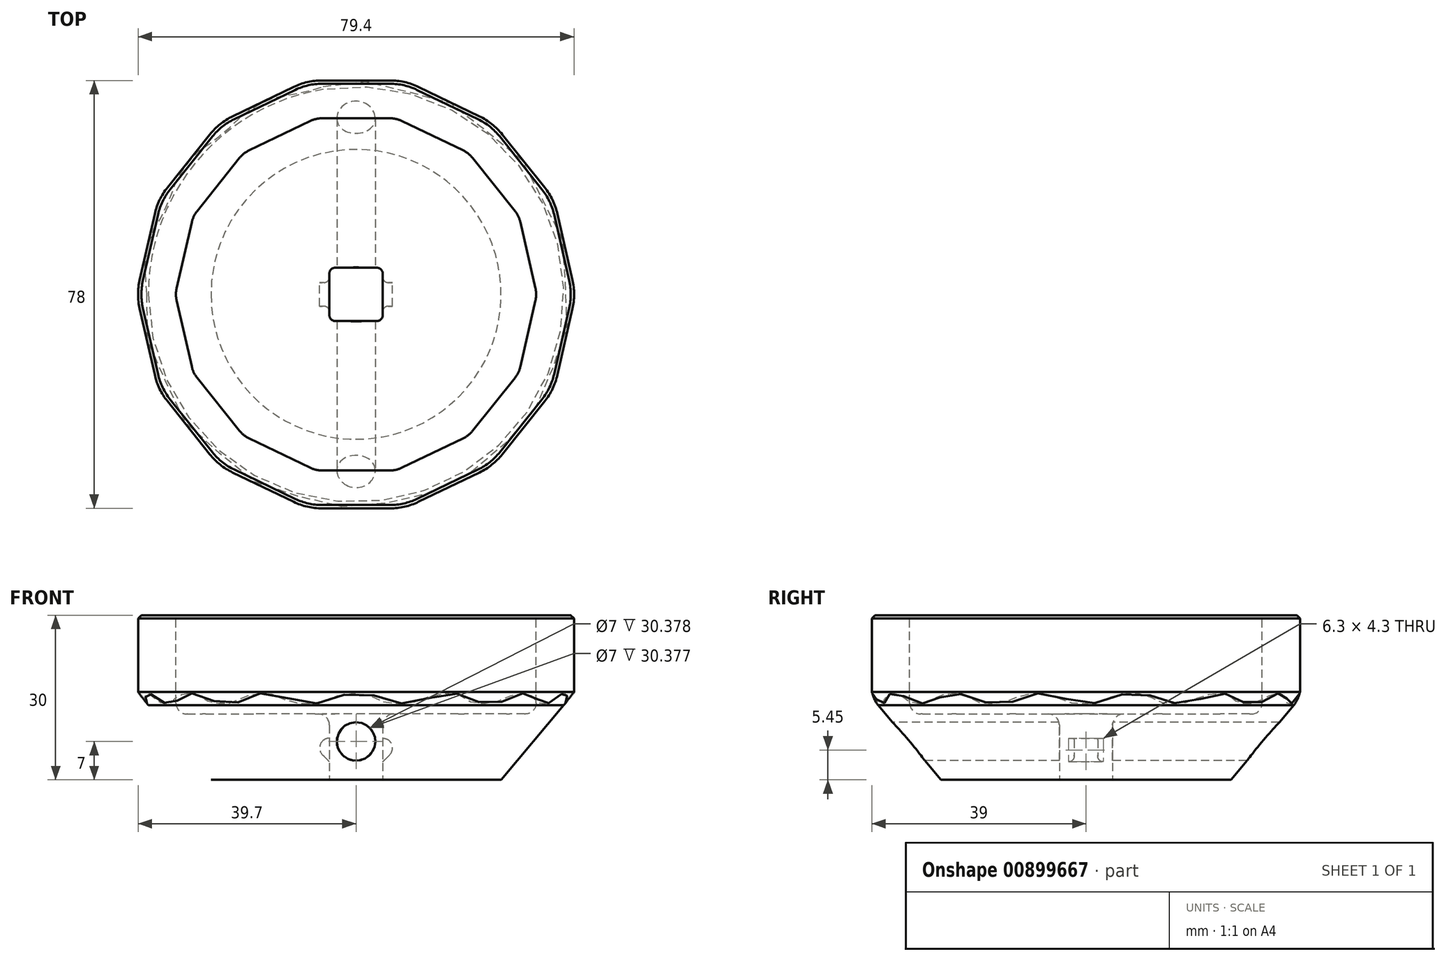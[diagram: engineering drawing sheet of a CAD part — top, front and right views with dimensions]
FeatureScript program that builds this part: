
annotation { "Feature Type Name" : "Feature", "Feature Type Description" : "" }
export const myFeature = defineFeature(function(context is Context, id is Id, definition is map)
    precondition{}
    {
        {
            var Q0;
            Q0=qCreatedBy(makeId("Top.planeOp"),FACE);
            var sketch = newSketch(context, id + "F0", { "sketchPlane" : qUnion([Q0])});
            skLineSegment(sketch, "E0.bottom", {"start": v(3.85, 4.85) * mm, "end": v(-3.85, 4.85) * mm});
            skLineSegment(sketch, "E0.top", {"start": v(3.85, -4.85) * mm, "end": v(-3.85, -4.85) * mm});
            skLineSegment(sketch, "E0.left", {"start": v(4.85, 3.85) * mm, "end": v(4.85, -3.85) * mm});
            skLineSegment(sketch, "E0.right", {"start": v(-4.85, 3.85) * mm, "end": v(-4.85, -3.85) * mm});
            skPoint(sketch, "E0.middle", {"position": v(0, 0) * mm});
            skPoint(sketch, "E1.visualSharp", {"position": v(-4.85, -4.85) * mm});
            skArc(sketch, "E1.filletArc", {"start": v(-4.85, -3.85) * mm, "mid": v(-4.56, -4.56) * mm, "end": v(-3.85, -4.85) * mm});
            skPoint(sketch, "E2.visualSharp", {"position": v(4.85, -4.85) * mm});
            skArc(sketch, "E2.filletArc", {"start": v(3.85, -4.85) * mm, "mid": v(4.56, -4.56) * mm, "end": v(4.85, -3.85) * mm});
            skPoint(sketch, "E3.visualSharp", {"position": v(4.85, 4.85) * mm});
            skArc(sketch, "E3.filletArc", {"start": v(4.85, 3.85) * mm, "mid": v(4.56, 4.56) * mm, "end": v(3.85, 4.85) * mm});
            skPoint(sketch, "E4.visualSharp", {"position": v(-4.85, 4.85) * mm});
            skArc(sketch, "E4.filletArc", {"start": v(-3.85, 4.85) * mm, "mid": v(-4.56, 4.56) * mm, "end": v(-4.85, 3.85) * mm});
            skSolve(sketch);
        }
        {
            var Q0;
            Q0=qCreatedBy(makeId("Front.planeOp"),FACE);
            var sketch = newSketch(context, id + "F1", { "sketchPlane" : qUnion([Q0])});
            skLineSegment(sketch, "E5", {"start": v(0, 0) * mm, "end": v(0, 30) * mm});
            skLineSegment(sketch, "E6", {"start": v(0, 30) * mm, "end": v(-39, 30) * mm});
            skLineSegment(sketch, "E7", {"start": v(-39, 30) * mm, "end": v(-39, 16.82) * mm});
            skLineSegment(sketch, "E8", {"start": v(-37.83, 13.6) * mm, "end": v(-26.41, 0) * mm});
            skLineSegment(sketch, "E9", {"start": v(-26.41, 0) * mm, "end": v(0, 0) * mm});
            skLineSegment(sketch, "E10", {"start": v(0, 0) * mm, "end": v(0, -5.87) * mm, "construction": true});
            skPoint(sketch, "E11.visualSharp", {"position": v(-39, 15) * mm});
            skArc(sketch, "E11.filletArc", {"start": v(-39, 16.82) * mm, "mid": v(-38.7, 15.1) * mm, "end": v(-37.83, 13.6) * mm});
            skSolve(sketch);
        }
        {
            var Q0;
            Q0=qSketchRegion(id+"F1",true);
            var Q1;
            Q1=sQuery(id+"F1.wireOp",EDGE,"E5");
            revolve(context, id + "F2", {"surfaceOperationType" : NewSurfaceOperationType.NEW, "entities" : qUnion([Q0]), "axis" : qUnion([Q1]), "revolveType" : RevolveType.FULL});
        }
        {
            var Q0;
            Q0=qSketchRegion(id+"F0",true);
            extrude(context, id + "F3", {"entities" : qUnion([Q0]), "operationType" : NewBodyOperationType.REMOVE, "endBound" : BoundingType.THROUGH_ALL, "depth" : 12 * mm, "offsetDistance" : 25 * mm});
        }
        {
            var Q0;
            Q0=makeQuery(id+"F2.opRevolve","SWEPT_FACE",FACE,{"disambiguationData":[OSD([sQuery(id+"F1.wireOp",EDGE,"E6")])]});
            var sketch = newSketch(context, id + "F4", { "sketchPlane" : qUnion([Q0])});
            skCircle(sketch, "E12.cCircle", {"center": v(0, 0) * mm, "radius": 32.93 * mm, "construction": true});
            skLineSegment(sketch, "E12.0", {"start": v(21.24, 24.85) * mm, "end": v(28.95, 15.18) * mm});
            skLineSegment(sketch, "E12.1", {"start": v(29.92, 13.17) * mm, "end": v(32.67, 1.11) * mm});
            skLineSegment(sketch, "E12.2", {"start": v(32.67, -1.11) * mm, "end": v(29.92, -13.17) * mm});
            skLineSegment(sketch, "E12.3", {"start": v(28.95, -15.18) * mm, "end": v(21.24, -24.85) * mm});
            skLineSegment(sketch, "E12.4", {"start": v(19.5, -26.24) * mm, "end": v(8.35, -31.6) * mm});
            skLineSegment(sketch, "E12.5", {"start": v(6.19, -32.1) * mm, "end": v(-6.19, -32.1) * mm});
            skLineSegment(sketch, "E12.6", {"start": v(-8.35, -31.6) * mm, "end": v(-19.5, -26.24) * mm});
            skLineSegment(sketch, "E12.7", {"start": v(-21.24, -24.85) * mm, "end": v(-28.95, -15.18) * mm});
            skLineSegment(sketch, "E12.8", {"start": v(-29.92, -13.17) * mm, "end": v(-32.67, -1.11) * mm});
            skLineSegment(sketch, "E12.9", {"start": v(-32.67, 1.11) * mm, "end": v(-29.92, 13.17) * mm});
            skLineSegment(sketch, "E12.10", {"start": v(-28.95, 15.18) * mm, "end": v(-21.24, 24.85) * mm});
            skLineSegment(sketch, "E12.11", {"start": v(-19.5, 26.24) * mm, "end": v(-8.35, 31.6) * mm});
            skLineSegment(sketch, "E12.12", {"start": v(-6.19, 32.1) * mm, "end": v(6.19, 32.1) * mm});
            skLineSegment(sketch, "E12.13", {"start": v(8.35, 31.6) * mm, "end": v(19.5, 26.24) * mm});
            skPoint(sketch, "E13.visualSharp", {"position": v(32.93, 0) * mm});
            skArc(sketch, "E13.filletArc", {"start": v(32.67, -1.11) * mm, "mid": v(32.8, 0) * mm, "end": v(32.67, 1.11) * mm});
            skPoint(sketch, "E14.visualSharp", {"position": v(29.66, -14.29) * mm});
            skArc(sketch, "E14.filletArc", {"start": v(28.95, -15.18) * mm, "mid": v(29.55, -14.23) * mm, "end": v(29.92, -13.17) * mm});
            skPoint(sketch, "E15.visualSharp", {"position": v(29.66, 14.29) * mm});
            skArc(sketch, "E15.filletArc", {"start": v(29.92, 13.17) * mm, "mid": v(29.55, 14.23) * mm, "end": v(28.95, 15.18) * mm});
            skPoint(sketch, "E16.visualSharp", {"position": v(20.53, 25.74) * mm});
            skArc(sketch, "E16.filletArc", {"start": v(21.24, 24.85) * mm, "mid": v(20.45, 25.64) * mm, "end": v(19.5, 26.24) * mm});
            skPoint(sketch, "E17.visualSharp", {"position": v(7.33, 32.1) * mm});
            skArc(sketch, "E17.filletArc", {"start": v(8.35, 31.6) * mm, "mid": v(7.3, 31.97) * mm, "end": v(6.19, 32.1) * mm});
            skPoint(sketch, "E18.visualSharp", {"position": v(-7.33, 32.1) * mm});
            skArc(sketch, "E18.filletArc", {"start": v(-6.19, 32.1) * mm, "mid": v(-7.3, 31.97) * mm, "end": v(-8.35, 31.6) * mm});
            skPoint(sketch, "E19.visualSharp", {"position": v(-20.53, 25.74) * mm});
            skArc(sketch, "E19.filletArc", {"start": v(-19.5, 26.24) * mm, "mid": v(-20.45, 25.64) * mm, "end": v(-21.24, 24.85) * mm});
            skPoint(sketch, "E20.visualSharp", {"position": v(-29.66, 14.29) * mm});
            skArc(sketch, "E20.filletArc", {"start": v(-28.95, 15.18) * mm, "mid": v(-29.55, 14.23) * mm, "end": v(-29.92, 13.17) * mm});
            skPoint(sketch, "E21.visualSharp", {"position": v(-32.93, 0) * mm});
            skArc(sketch, "E21.filletArc", {"start": v(-32.67, 1.11) * mm, "mid": v(-32.8, 0) * mm, "end": v(-32.67, -1.11) * mm});
            skPoint(sketch, "E22.visualSharp", {"position": v(-29.66, -14.29) * mm});
            skArc(sketch, "E22.filletArc", {"start": v(-29.92, -13.17) * mm, "mid": v(-29.55, -14.23) * mm, "end": v(-28.95, -15.18) * mm});
            skPoint(sketch, "E23.visualSharp", {"position": v(-20.53, -25.74) * mm});
            skArc(sketch, "E23.filletArc", {"start": v(-21.24, -24.85) * mm, "mid": v(-20.45, -25.64) * mm, "end": v(-19.5, -26.24) * mm});
            skPoint(sketch, "E24.visualSharp", {"position": v(-7.33, -32.1) * mm});
            skArc(sketch, "E24.filletArc", {"start": v(-8.35, -31.6) * mm, "mid": v(-7.3, -31.97) * mm, "end": v(-6.19, -32.1) * mm});
            skPoint(sketch, "E25.visualSharp", {"position": v(7.33, -32.1) * mm});
            skArc(sketch, "E25.filletArc", {"start": v(6.19, -32.1) * mm, "mid": v(7.3, -31.97) * mm, "end": v(8.35, -31.6) * mm});
            skPoint(sketch, "E26.visualSharp", {"position": v(20.53, -25.74) * mm});
            skArc(sketch, "E26.filletArc", {"start": v(19.5, -26.24) * mm, "mid": v(20.45, -25.64) * mm, "end": v(21.24, -24.85) * mm});
            skSolve(sketch);
        }
        {
            var Q0;
            Q0=makeQuery(id+"F4.imprint","IMPRINT",FACE,{"disambiguationData":[TD([[makeQuery(id+"F4.imprint","IMPRINT",EDGE,{"derivedFrom":sQuery(id+"F4.wireOp",EDGE,"E12.0")}),1.0]])]});
            var sketch = newSketch(context, id + "F5", { "sketchPlane" : qUnion([Q0])});
            skCircle(sketch, "E27.0", {"center": v(0, 0) * mm, "radius": 32.93 * mm, "construction": true});
            skLineSegment(sketch, "E27.1", {"start": v(21.24, 24.85) * mm, "end": v(28.95, 15.18) * mm});
            skLineSegment(sketch, "E27.2", {"start": v(29.92, 13.17) * mm, "end": v(32.67, 1.11) * mm});
            skLineSegment(sketch, "E27.3", {"start": v(32.67, -1.11) * mm, "end": v(29.92, -13.17) * mm});
            skLineSegment(sketch, "E27.4", {"start": v(28.95, -15.18) * mm, "end": v(21.24, -24.85) * mm});
            skLineSegment(sketch, "E27.5", {"start": v(19.5, -26.24) * mm, "end": v(8.35, -31.6) * mm});
            skLineSegment(sketch, "E27.6", {"start": v(6.19, -32.1) * mm, "end": v(-6.19, -32.1) * mm});
            skLineSegment(sketch, "E27.7", {"start": v(-8.35, -31.6) * mm, "end": v(-19.5, -26.24) * mm});
            skLineSegment(sketch, "E27.8", {"start": v(-21.24, -24.85) * mm, "end": v(-28.95, -15.18) * mm});
            skLineSegment(sketch, "E27.9", {"start": v(-29.92, -13.17) * mm, "end": v(-32.67, -1.11) * mm});
            skLineSegment(sketch, "E27.10", {"start": v(-32.67, 1.11) * mm, "end": v(-29.92, 13.17) * mm});
            skLineSegment(sketch, "E27.11", {"start": v(-28.95, 15.18) * mm, "end": v(-21.24, 24.85) * mm});
            skLineSegment(sketch, "E27.12", {"start": v(-19.5, 26.24) * mm, "end": v(-8.35, 31.6) * mm});
            skLineSegment(sketch, "E27.13", {"start": v(-6.19, 32.1) * mm, "end": v(6.19, 32.1) * mm});
            skLineSegment(sketch, "E27.14", {"start": v(8.35, 31.6) * mm, "end": v(19.5, 26.24) * mm});
            skPoint(sketch, "E27.15", {"position": v(32.93, 0) * mm});
            skArc(sketch, "E27.16", {"start": v(32.67, -1.11) * mm, "mid": v(32.8, 0) * mm, "end": v(32.67, 1.11) * mm});
            skPoint(sketch, "E27.17", {"position": v(29.66, -14.29) * mm});
            skArc(sketch, "E27.18", {"start": v(28.95, -15.18) * mm, "mid": v(29.55, -14.23) * mm, "end": v(29.92, -13.17) * mm});
            skPoint(sketch, "E27.19", {"position": v(29.66, 14.29) * mm});
            skArc(sketch, "E27.20", {"start": v(29.92, 13.17) * mm, "mid": v(29.55, 14.23) * mm, "end": v(28.95, 15.18) * mm});
            skPoint(sketch, "E27.21", {"position": v(20.53, 25.74) * mm});
            skArc(sketch, "E27.22", {"start": v(21.24, 24.85) * mm, "mid": v(20.45, 25.64) * mm, "end": v(19.5, 26.24) * mm});
            skPoint(sketch, "E27.23", {"position": v(7.33, 32.1) * mm});
            skArc(sketch, "E27.24", {"start": v(8.35, 31.6) * mm, "mid": v(7.3, 31.97) * mm, "end": v(6.19, 32.1) * mm});
            skPoint(sketch, "E27.25", {"position": v(-7.33, 32.1) * mm});
            skArc(sketch, "E27.26", {"start": v(-6.19, 32.1) * mm, "mid": v(-7.3, 31.97) * mm, "end": v(-8.35, 31.6) * mm});
            skPoint(sketch, "E27.27", {"position": v(-20.53, 25.74) * mm});
            skArc(sketch, "E27.28", {"start": v(-19.5, 26.24) * mm, "mid": v(-20.45, 25.64) * mm, "end": v(-21.24, 24.85) * mm});
            skPoint(sketch, "E27.29", {"position": v(-29.66, 14.29) * mm});
            skArc(sketch, "E27.30", {"start": v(-28.95, 15.18) * mm, "mid": v(-29.55, 14.23) * mm, "end": v(-29.92, 13.17) * mm});
            skPoint(sketch, "E27.31", {"position": v(-32.93, 0) * mm});
            skArc(sketch, "E27.32", {"start": v(-32.67, 1.11) * mm, "mid": v(-32.8, 0) * mm, "end": v(-32.67, -1.11) * mm});
            skPoint(sketch, "E27.33", {"position": v(-29.66, -14.29) * mm});
            skArc(sketch, "E27.34", {"start": v(-29.92, -13.17) * mm, "mid": v(-29.55, -14.23) * mm, "end": v(-28.95, -15.18) * mm});
            skPoint(sketch, "E27.35", {"position": v(-20.53, -25.74) * mm});
            skArc(sketch, "E27.36", {"start": v(-21.24, -24.85) * mm, "mid": v(-20.45, -25.64) * mm, "end": v(-19.5, -26.24) * mm});
            skPoint(sketch, "E27.37", {"position": v(-7.33, -32.1) * mm});
            skArc(sketch, "E27.38", {"start": v(-8.35, -31.6) * mm, "mid": v(-7.3, -31.97) * mm, "end": v(-6.19, -32.1) * mm});
            skPoint(sketch, "E27.39", {"position": v(7.33, -32.1) * mm});
            skArc(sketch, "E27.40", {"start": v(6.19, -32.1) * mm, "mid": v(7.3, -31.97) * mm, "end": v(8.35, -31.6) * mm});
            skPoint(sketch, "E27.41", {"position": v(20.53, -25.74) * mm});
            skArc(sketch, "E27.42", {"start": v(19.5, -26.24) * mm, "mid": v(20.45, -25.64) * mm, "end": v(21.24, -24.85) * mm});
            skArc(sketch, "E28.0", {"start": v(-6.19, 39) * mm, "mid": v(-8.83, 38.7) * mm, "end": v(-11.35, 37.82) * mm});
            skLineSegment(sketch, "E28.1", {"start": v(-22.5, 32.45) * mm, "end": v(-11.35, 37.82) * mm});
            skArc(sketch, "E28.2", {"start": v(-22.5, 32.45) * mm, "mid": v(-24.75, 31.04) * mm, "end": v(-26.63, 29.15) * mm});
            skLineSegment(sketch, "E28.3", {"start": v(-34.35, 19.48) * mm, "end": v(-26.63, 29.15) * mm});
            skArc(sketch, "E28.4", {"start": v(-34.35, 19.48) * mm, "mid": v(-35.77, 17.22) * mm, "end": v(-36.65, 14.7) * mm});
            skLineSegment(sketch, "E28.5", {"start": v(34.35, -19.48) * mm, "end": v(26.63, -29.15) * mm});
            skArc(sketch, "E28.6", {"start": v(34.35, -19.48) * mm, "mid": v(35.77, -17.22) * mm, "end": v(36.65, -14.7) * mm});
            skLineSegment(sketch, "E28.7", {"start": v(39.4, -2.65) * mm, "end": v(36.65, -14.7) * mm});
            skArc(sketch, "E28.8", {"start": v(39.4, -2.65) * mm, "mid": v(39.7, 0) * mm, "end": v(39.4, 2.65) * mm});
            skLineSegment(sketch, "E28.9", {"start": v(36.65, 14.7) * mm, "end": v(39.4, 2.65) * mm});
            skArc(sketch, "E28.10", {"start": v(36.65, 14.7) * mm, "mid": v(35.77, 17.22) * mm, "end": v(34.35, 19.48) * mm});
            skArc(sketch, "E28.11", {"start": v(11.35, 37.82) * mm, "mid": v(8.83, 38.7) * mm, "end": v(6.19, 39) * mm});
            skLineSegment(sketch, "E28.12", {"start": v(11.35, 37.82) * mm, "end": v(22.5, 32.45) * mm});
            skArc(sketch, "E28.13", {"start": v(26.63, 29.15) * mm, "mid": v(24.75, 31.04) * mm, "end": v(22.5, 32.45) * mm});
            skLineSegment(sketch, "E28.14", {"start": v(26.63, 29.15) * mm, "end": v(34.35, 19.48) * mm});
            skArc(sketch, "E28.15", {"start": v(22.5, -32.45) * mm, "mid": v(24.75, -31.04) * mm, "end": v(26.63, -29.15) * mm});
            skLineSegment(sketch, "E28.16", {"start": v(22.5, -32.45) * mm, "end": v(11.35, -37.82) * mm});
            skArc(sketch, "E28.17", {"start": v(6.19, -39) * mm, "mid": v(8.83, -38.7) * mm, "end": v(11.35, -37.82) * mm});
            skLineSegment(sketch, "E28.18", {"start": v(6.19, -39) * mm, "end": v(-6.19, -39) * mm});
            skArc(sketch, "E28.19", {"start": v(-11.35, -37.82) * mm, "mid": v(-8.83, -38.7) * mm, "end": v(-6.19, -39) * mm});
            skLineSegment(sketch, "E28.20", {"start": v(-6.19, 39) * mm, "end": v(6.19, 39) * mm});
            skLineSegment(sketch, "E28.21", {"start": v(-11.35, -37.82) * mm, "end": v(-22.5, -32.45) * mm});
            skArc(sketch, "E28.22", {"start": v(-26.63, -29.15) * mm, "mid": v(-24.75, -31.04) * mm, "end": v(-22.5, -32.45) * mm});
            skLineSegment(sketch, "E28.23", {"start": v(-26.63, -29.15) * mm, "end": v(-34.35, -19.48) * mm});
            skArc(sketch, "E28.24", {"start": v(-36.65, -14.7) * mm, "mid": v(-35.77, -17.22) * mm, "end": v(-34.35, -19.48) * mm});
            skLineSegment(sketch, "E28.25", {"start": v(-36.65, -14.7) * mm, "end": v(-39.4, -2.65) * mm});
            skArc(sketch, "E28.26", {"start": v(-39.4, 2.65) * mm, "mid": v(-39.7, 0) * mm, "end": v(-39.4, -2.65) * mm});
            skLineSegment(sketch, "E28.27", {"start": v(-39.4, 2.65) * mm, "end": v(-36.65, 14.7) * mm});
            skSolve(sketch);
        }
        {
            var Q0;
            Q0=qCreatedBy(makeId("Top.planeOp"),FACE);
            var Q1;
            Q1=sQuery(id+"F1.wireOp",VERTEX,"E8.start");
            cPlane(context, id + "F6", {"entities" : qUnion([Q0, Q1]), "cplaneType" : CPlaneType.PLANE_POINT, "offset" : 25 * mm, "width" : 150 * mm, "height" : 150 * mm});
        }
        {
            var Q0;
            Q0=qSketchRegion(id+"F5",true);
            var Q1;
            Q1=makeQuery(id+"F11.boolean.opBoolean","COPY",FACE,{"derivedFrom":makeQuery(id+"F11.opExtrude","CAP_FACE",FACE,{"disambiguationData":[OSD([sQuery(id+"F4.wireOp",EDGE,"E12.0"),sQuery(id+"F4.wireOp",EDGE,"E12.1"),sQuery(id+"F4.wireOp",EDGE,"E12.2"),sQuery(id+"F4.wireOp",EDGE,"E12.3"),sQuery(id+"F4.wireOp",EDGE,"E12.4"),sQuery(id+"F4.wireOp",EDGE,"E12.5"),sQuery(id+"F4.wireOp",EDGE,"E12.6"),sQuery(id+"F4.wireOp",EDGE,"E12.7"),sQuery(id+"F4.wireOp",EDGE,"E12.8"),sQuery(id+"F4.wireOp",EDGE,"E12.9"),sQuery(id+"F4.wireOp",EDGE,"E12.10"),sQuery(id+"F4.wireOp",EDGE,"E12.11"),sQuery(id+"F4.wireOp",EDGE,"E12.12"),sQuery(id+"F4.wireOp",EDGE,"E12.13"),sQuery(id+"F4.wireOp",EDGE,"E13.filletArc"),sQuery(id+"F4.wireOp",EDGE,"E14.filletArc"),sQuery(id+"F4.wireOp",EDGE,"E15.filletArc"),sQuery(id+"F4.wireOp",EDGE,"E16.filletArc"),sQuery(id+"F4.wireOp",EDGE,"E17.filletArc"),sQuery(id+"F4.wireOp",EDGE,"E18.filletArc"),sQuery(id+"F4.wireOp",EDGE,"E19.filletArc"),sQuery(id+"F4.wireOp",EDGE,"E20.filletArc"),sQuery(id+"F4.wireOp",EDGE,"E21.filletArc"),sQuery(id+"F4.wireOp",EDGE,"E22.filletArc"),sQuery(id+"F4.wireOp",EDGE,"E23.filletArc"),sQuery(id+"F4.wireOp",EDGE,"E24.filletArc"),sQuery(id+"F4.wireOp",EDGE,"E25.filletArc"),sQuery(id+"F4.wireOp",EDGE,"E26.filletArc")])],"isStart":false})});
            extrude(context, id + "F7", {"entities" : qUnion([Q0]), "operationType" : NewBodyOperationType.ADD, "oppositeDirection" : true, "depth" : 14 * mm, "endBoundEntityFace" : qUnion([Q1]), "offsetDistance" : 25 * mm});
        }
        {
            var Q0;
            Q0=qCreatedBy(id+"F6.planeOp",FACE);
            var sketch = newSketch(context, id + "F8", { "sketchPlane" : qUnion([Q0])});
            skCircle(sketch, "E29.0", {"center": v(0, 0) * mm, "radius": 37.83 * mm});
            skLineSegment(sketch, "E30", {"start": v(6.19, 39) * mm, "end": v(0, 0) * mm, "construction": true});
            skLineSegment(sketch, "E31", {"start": v(0, 0) * mm, "end": v(11.35, 37.82) * mm, "construction": true});
            skPoint(sketch, "E32.0", {"position": v(11.35, 37.82) * mm});
            skPoint(sketch, "E33.1", {"position": v(6.19, 39) * mm});
            skPoint(sketch, "E34", {"position": v(10.87, 36.23) * mm});
            skPoint(sketch, "E35", {"position": v(5.93, 37.36) * mm});
            skPoint(sketch, "E36.1.0", {"position": v(-5.93, 37.36) * mm});
            skPoint(sketch, "E36.1.1", {"position": v(-10.87, 36.23) * mm});
            skPoint(sketch, "E36.2.0", {"position": v(-21.55, 31.1) * mm});
            skPoint(sketch, "E36.2.1", {"position": v(-25.52, 27.93) * mm});
            skPoint(sketch, "E36.3.0", {"position": v(-32.9, 18.66) * mm});
            skPoint(sketch, "E36.3.1", {"position": v(-35.1, 14.1) * mm});
            skPoint(sketch, "E36.4.0", {"position": v(-37.75, 2.54) * mm});
            skPoint(sketch, "E36.4.1", {"position": v(-37.75, -2.54) * mm});
            skPoint(sketch, "E36.5.0", {"position": v(-35.1, -14.1) * mm});
            skPoint(sketch, "E36.5.1", {"position": v(-32.9, -18.66) * mm});
            skPoint(sketch, "E36.6.0", {"position": v(-25.52, -27.93) * mm});
            skPoint(sketch, "E36.6.1", {"position": v(-21.55, -31.1) * mm});
            skPoint(sketch, "E36.7.0", {"position": v(-10.87, -36.23) * mm});
            skPoint(sketch, "E36.7.1", {"position": v(-5.93, -37.36) * mm});
            skPoint(sketch, "E36.8.0", {"position": v(5.93, -37.36) * mm});
            skPoint(sketch, "E36.8.1", {"position": v(10.87, -36.23) * mm});
            skPoint(sketch, "E36.9.0", {"position": v(21.55, -31.1) * mm});
            skPoint(sketch, "E36.9.1", {"position": v(25.52, -27.93) * mm});
            skPoint(sketch, "E36.10.0", {"position": v(32.9, -18.66) * mm});
            skPoint(sketch, "E36.10.1", {"position": v(35.1, -14.1) * mm});
            skPoint(sketch, "E36.11.0", {"position": v(37.75, -2.54) * mm});
            skPoint(sketch, "E36.11.1", {"position": v(37.75, 2.54) * mm});
            skPoint(sketch, "E36.12.0", {"position": v(35.1, 14.1) * mm});
            skPoint(sketch, "E36.12.1", {"position": v(32.9, 18.66) * mm});
            skPoint(sketch, "E36.13.0", {"position": v(25.52, 27.93) * mm});
            skPoint(sketch, "E36.13.1", {"position": v(21.55, 31.1) * mm});
            skSolve(sketch);
        }
        {
            var Q0;
            Q0=makeQuery(id+"F7.opExtrude","CAP_FACE",FACE,{"disambiguationData":[OSD([sQuery(id+"F5.wireOp",EDGE,"E27.1"),sQuery(id+"F5.wireOp",EDGE,"E27.2"),sQuery(id+"F5.wireOp",EDGE,"E27.3"),sQuery(id+"F5.wireOp",EDGE,"E27.4"),sQuery(id+"F5.wireOp",EDGE,"E27.5"),sQuery(id+"F5.wireOp",EDGE,"E27.6"),sQuery(id+"F5.wireOp",EDGE,"E27.7"),sQuery(id+"F5.wireOp",EDGE,"E27.8"),sQuery(id+"F5.wireOp",EDGE,"E27.9"),sQuery(id+"F5.wireOp",EDGE,"E27.10"),sQuery(id+"F5.wireOp",EDGE,"E27.11"),sQuery(id+"F5.wireOp",EDGE,"E27.12"),sQuery(id+"F5.wireOp",EDGE,"E27.13"),sQuery(id+"F5.wireOp",EDGE,"E27.14"),sQuery(id+"F5.wireOp",EDGE,"E27.16"),sQuery(id+"F5.wireOp",EDGE,"E27.18"),sQuery(id+"F5.wireOp",EDGE,"E27.20"),sQuery(id+"F5.wireOp",EDGE,"E27.22"),sQuery(id+"F5.wireOp",EDGE,"E27.24"),sQuery(id+"F5.wireOp",EDGE,"E27.26"),sQuery(id+"F5.wireOp",EDGE,"E27.28"),sQuery(id+"F5.wireOp",EDGE,"E27.30"),sQuery(id+"F5.wireOp",EDGE,"E27.32"),sQuery(id+"F5.wireOp",EDGE,"E27.34"),sQuery(id+"F5.wireOp",EDGE,"E27.36"),sQuery(id+"F5.wireOp",EDGE,"E27.38"),sQuery(id+"F5.wireOp",EDGE,"E27.40"),sQuery(id+"F5.wireOp",EDGE,"E27.42"),sQuery(id+"F5.wireOp",EDGE,"E28.0"),sQuery(id+"F5.wireOp",EDGE,"E28.1"),sQuery(id+"F5.wireOp",EDGE,"E28.2"),sQuery(id+"F5.wireOp",EDGE,"E28.3"),sQuery(id+"F5.wireOp",EDGE,"E28.4"),sQuery(id+"F5.wireOp",EDGE,"E28.5"),sQuery(id+"F5.wireOp",EDGE,"E28.6"),sQuery(id+"F5.wireOp",EDGE,"E28.7"),sQuery(id+"F5.wireOp",EDGE,"E28.8"),sQuery(id+"F5.wireOp",EDGE,"E28.9"),sQuery(id+"F5.wireOp",EDGE,"E28.10"),sQuery(id+"F5.wireOp",EDGE,"E28.11"),sQuery(id+"F5.wireOp",EDGE,"E28.12"),sQuery(id+"F5.wireOp",EDGE,"E28.13"),sQuery(id+"F5.wireOp",EDGE,"E28.14"),sQuery(id+"F5.wireOp",EDGE,"E28.15"),sQuery(id+"F5.wireOp",EDGE,"E28.16"),sQuery(id+"F5.wireOp",EDGE,"E28.17"),sQuery(id+"F5.wireOp",EDGE,"E28.18"),sQuery(id+"F5.wireOp",EDGE,"E28.19"),sQuery(id+"F5.wireOp",EDGE,"E28.20"),sQuery(id+"F5.wireOp",EDGE,"E28.21"),sQuery(id+"F5.wireOp",EDGE,"E28.22"),sQuery(id+"F5.wireOp",EDGE,"E28.23"),sQuery(id+"F5.wireOp",EDGE,"E28.24"),sQuery(id+"F5.wireOp",EDGE,"E28.25"),sQuery(id+"F5.wireOp",EDGE,"E28.26"),sQuery(id+"F5.wireOp",EDGE,"E28.27")])],"isStart":false});
            var sketch = newSketch(context, id + "F9", { "sketchPlane" : qUnion([Q0])});
            skArc(sketch, "E37.43", {"start": v(-6.19, -39) * mm, "mid": v(-8.83, -38.7) * mm, "end": v(-11.35, -37.82) * mm});
            skLineSegment(sketch, "E37.44", {"start": v(-22.5, -32.45) * mm, "end": v(-11.35, -37.82) * mm});
            skArc(sketch, "E37.45", {"start": v(-22.5, -32.45) * mm, "mid": v(-24.75, -31.04) * mm, "end": v(-26.63, -29.15) * mm});
            skLineSegment(sketch, "E37.46", {"start": v(-34.35, -19.48) * mm, "end": v(-26.63, -29.15) * mm});
            skArc(sketch, "E37.47", {"start": v(-34.35, -19.48) * mm, "mid": v(-35.77, -17.22) * mm, "end": v(-36.65, -14.7) * mm});
            skLineSegment(sketch, "E37.48", {"start": v(34.35, 19.48) * mm, "end": v(26.63, 29.15) * mm});
            skArc(sketch, "E37.49", {"start": v(34.35, 19.48) * mm, "mid": v(35.77, 17.22) * mm, "end": v(36.65, 14.7) * mm});
            skLineSegment(sketch, "E37.50", {"start": v(39.4, 2.65) * mm, "end": v(36.65, 14.7) * mm});
            skArc(sketch, "E37.51", {"start": v(39.4, 2.65) * mm, "mid": v(39.7, 0) * mm, "end": v(39.4, -2.65) * mm});
            skLineSegment(sketch, "E37.52", {"start": v(36.65, -14.7) * mm, "end": v(39.4, -2.65) * mm});
            skArc(sketch, "E37.53", {"start": v(36.65, -14.7) * mm, "mid": v(35.77, -17.22) * mm, "end": v(34.35, -19.48) * mm});
            skArc(sketch, "E37.54", {"start": v(11.35, -37.82) * mm, "mid": v(8.83, -38.7) * mm, "end": v(6.19, -39) * mm});
            skLineSegment(sketch, "E37.55", {"start": v(11.35, -37.82) * mm, "end": v(22.5, -32.45) * mm});
            skArc(sketch, "E37.56", {"start": v(26.63, -29.15) * mm, "mid": v(24.75, -31.04) * mm, "end": v(22.5, -32.45) * mm});
            skLineSegment(sketch, "E37.57", {"start": v(26.63, -29.15) * mm, "end": v(34.35, -19.48) * mm});
            skArc(sketch, "E37.58", {"start": v(22.5, 32.45) * mm, "mid": v(24.75, 31.04) * mm, "end": v(26.63, 29.15) * mm});
            skLineSegment(sketch, "E37.59", {"start": v(22.5, 32.45) * mm, "end": v(11.35, 37.82) * mm});
            skArc(sketch, "E37.60", {"start": v(6.19, 39) * mm, "mid": v(8.83, 38.7) * mm, "end": v(11.35, 37.82) * mm});
            skLineSegment(sketch, "E37.61", {"start": v(6.19, 39) * mm, "end": v(-6.19, 39) * mm});
            skArc(sketch, "E37.62", {"start": v(-11.35, 37.82) * mm, "mid": v(-8.83, 38.7) * mm, "end": v(-6.19, 39) * mm});
            skLineSegment(sketch, "E37.63", {"start": v(-6.19, -39) * mm, "end": v(6.19, -39) * mm});
            skLineSegment(sketch, "E37.64", {"start": v(-11.35, 37.82) * mm, "end": v(-22.5, 32.45) * mm});
            skArc(sketch, "E37.65", {"start": v(-26.63, 29.15) * mm, "mid": v(-24.75, 31.04) * mm, "end": v(-22.5, 32.45) * mm});
            skLineSegment(sketch, "E37.66", {"start": v(-26.63, 29.15) * mm, "end": v(-34.35, 19.48) * mm});
            skArc(sketch, "E37.67", {"start": v(-36.65, 14.7) * mm, "mid": v(-35.77, 17.22) * mm, "end": v(-34.35, 19.48) * mm});
            skLineSegment(sketch, "E37.68", {"start": v(-36.65, 14.7) * mm, "end": v(-39.4, 2.65) * mm});
            skArc(sketch, "E37.69", {"start": v(-39.4, -2.65) * mm, "mid": v(-39.7, 0) * mm, "end": v(-39.4, 2.65) * mm});
            skLineSegment(sketch, "E37.70", {"start": v(-39.4, -2.65) * mm, "end": v(-36.65, -14.7) * mm});
            skSolve(sketch);
        }
        {
            var Q1;
            Q1=qSketchRegion(id+"F9",true);
            var Q2;
            Q2=qSketchRegion(id+"F8",true);
            loft(context, id + "F10", {"operationType" : NewBodyOperationType.ADD, "sheetProfilesArray" : [{ "sheetProfileEntities" : qUnion([Q1]) }, { "sheetProfileEntities" : qUnion([Q2]) }]});
        }
        {
            var Q0;
            Q0=qSketchRegion(id+"F4",true);
            extrude(context, id + "F11", {"entities" : qUnion([Q0]), "operationType" : NewBodyOperationType.REMOVE, "oppositeDirection" : true, "depth" : 18 * mm, "offsetDistance" : 25 * mm});
        }
        {
            var Q0;
            Q0=qCreatedBy(makeId("Front.planeOp"),FACE);
            var sketch = newSketch(context, id + "F12", { "sketchPlane" : qUnion([Q0])});
            skLineSegment(sketch, "E38", {"start": v(-4.85, 7.6) * mm, "end": v(0, 7.6) * mm});
            skLineSegment(sketch, "E39", {"start": v(-4.85, 3.3) * mm, "end": v(0, 3.3) * mm});
            skLineSegment(sketch, "E40", {"start": v(-5.67, 5.45) * mm, "end": v(-0.86, 5.45) * mm, "construction": true});
            skLineSegment(sketch, "E41", {"start": v(-4.85, 3.3) * mm, "end": v(-6.1, 4.56) * mm});
            skArc(sketch, "E42", {"start": v(-4.85, 7.6) * mm, "mid": v(-6.5, 6.5) * mm, "end": v(-6.1, 4.56) * mm});
            skLineSegment(sketch, "E43.MirrorCS", {"start": v(4.85, 7.6) * mm, "end": v(0, 7.6) * mm});
            skArc(sketch, "E44.MirrorCS", {"start": v(4.85, 7.6) * mm, "mid": v(6.5, 6.5) * mm, "end": v(6.1, 4.56) * mm});
            skLineSegment(sketch, "E45.MirrorCS", {"start": v(4.85, 3.3) * mm, "end": v(6.1, 4.56) * mm});
            skLineSegment(sketch, "E46.MirrorCS", {"start": v(4.85, 3.3) * mm, "end": v(0, 3.3) * mm});
            skLineSegment(sketch, "E47.MirrorCS", {"start": v(5.67, 5.45) * mm, "end": v(0.86, 5.45) * mm, "construction": true});
            skSolve(sketch);
        }
        {
            var Q0;
            Q0=qSketchRegion(id+"F12",true);
            extrude(context, id + "F13", {"entities" : qUnion([Q0]), "operationType" : NewBodyOperationType.REMOVE, "endBound" : BoundingType.SYMMETRIC, "depth" : 4.3 * mm, "offsetDistance" : 25 * mm});
        }
        {
            var Q0;
            Q0=makeQuery(id+"F13.boolean.opBoolean","INTERSECT",EDGE,{"derivedFrom":[makeQuery(id+"F3.boolean.opBoolean","COPY",FACE,{"derivedFrom":makeQuery(id+"F3.opExtrude","SWEPT_FACE",FACE,{"disambiguationData":[OSD([sQuery(id+"F0.wireOp",EDGE,"E0.right")])]})}),makeQuery(id+"F13.opExtrude","CAP_FACE",FACE,{"disambiguationData":[OSD([sQuery(id+"F12.wireOp",EDGE,"E38"),sQuery(id+"F12.wireOp",EDGE,"E39"),sQuery(id+"F12.wireOp",EDGE,"E41"),sQuery(id+"F12.wireOp",EDGE,"E42"),sQuery(id+"F12.wireOp",EDGE,"E43.MirrorCS"),sQuery(id+"F12.wireOp",EDGE,"E44.MirrorCS"),sQuery(id+"F12.wireOp",EDGE,"E45.MirrorCS"),sQuery(id+"F12.wireOp",EDGE,"E46.MirrorCS")])],"isStart":false})]});
            var Q1;
            Q1=makeQuery(id+"FJ3eJoukwGj3lDz_1.1.F13.boolean.opBoolean","INTERSECT",EDGE,{"derivedFrom":[makeQuery(id+"F3.boolean.opBoolean","COPY",FACE,{"derivedFrom":makeQuery(id+"F3.opExtrude","SWEPT_FACE",FACE,{"disambiguationData":[OSD([sQuery(id+"F0.wireOp",EDGE,"E0.top")])]})}),makeQuery(id+"FJ3eJoukwGj3lDz_1.1.F13.opExtrude","CAP_FACE",FACE,{"disambiguationData":[OSD([sQuery(id+"F12.wireOp",EDGE,"E38"),sQuery(id+"F12.wireOp",EDGE,"E39"),sQuery(id+"F12.wireOp",EDGE,"E41"),sQuery(id+"F12.wireOp",EDGE,"E42"),sQuery(id+"F12.wireOp",EDGE,"E43.MirrorCS"),sQuery(id+"F12.wireOp",EDGE,"E44.MirrorCS"),sQuery(id+"F12.wireOp",EDGE,"E45.MirrorCS"),sQuery(id+"F12.wireOp",EDGE,"E46.MirrorCS")])],"isStart":true})]});
            var Q2;
            Q2=makeQuery(id+"F13.boolean.opBoolean","INTERSECT",EDGE,{"derivedFrom":[makeQuery(id+"F3.boolean.opBoolean","COPY",FACE,{"derivedFrom":makeQuery(id+"F3.opExtrude","SWEPT_FACE",FACE,{"disambiguationData":[OSD([sQuery(id+"F0.wireOp",EDGE,"E0.right")])]})}),makeQuery(id+"F13.opExtrude","CAP_FACE",FACE,{"disambiguationData":[OSD([sQuery(id+"F12.wireOp",EDGE,"E38"),sQuery(id+"F12.wireOp",EDGE,"E39"),sQuery(id+"F12.wireOp",EDGE,"E41"),sQuery(id+"F12.wireOp",EDGE,"E42"),sQuery(id+"F12.wireOp",EDGE,"E43.MirrorCS"),sQuery(id+"F12.wireOp",EDGE,"E44.MirrorCS"),sQuery(id+"F12.wireOp",EDGE,"E45.MirrorCS"),sQuery(id+"F12.wireOp",EDGE,"E46.MirrorCS")])],"isStart":true})]});
            var Q3;
            Q3=makeQuery(id+"FJ3eJoukwGj3lDz_1.1.F13.boolean.opBoolean","INTERSECT",EDGE,{"derivedFrom":[makeQuery(id+"F3.boolean.opBoolean","COPY",FACE,{"derivedFrom":makeQuery(id+"F3.opExtrude","SWEPT_FACE",FACE,{"disambiguationData":[OSD([sQuery(id+"F0.wireOp",EDGE,"E0.bottom")])]})}),makeQuery(id+"FJ3eJoukwGj3lDz_1.1.F13.opExtrude","CAP_FACE",FACE,{"disambiguationData":[OSD([sQuery(id+"F12.wireOp",EDGE,"E38"),sQuery(id+"F12.wireOp",EDGE,"E39"),sQuery(id+"F12.wireOp",EDGE,"E41"),sQuery(id+"F12.wireOp",EDGE,"E42"),sQuery(id+"F12.wireOp",EDGE,"E43.MirrorCS"),sQuery(id+"F12.wireOp",EDGE,"E44.MirrorCS"),sQuery(id+"F12.wireOp",EDGE,"E45.MirrorCS"),sQuery(id+"F12.wireOp",EDGE,"E46.MirrorCS")])],"isStart":true})]});
            var Q4;
            Q4=makeQuery(id+"FJ3eJoukwGj3lDz_1.1.F13.boolean.opBoolean","INTERSECT",EDGE,{"derivedFrom":[makeQuery(id+"F3.boolean.opBoolean","COPY",FACE,{"derivedFrom":makeQuery(id+"F3.opExtrude","SWEPT_FACE",FACE,{"disambiguationData":[OSD([sQuery(id+"F0.wireOp",EDGE,"E0.bottom")])]})}),makeQuery(id+"FJ3eJoukwGj3lDz_1.1.F13.opExtrude","CAP_FACE",FACE,{"disambiguationData":[OSD([sQuery(id+"F12.wireOp",EDGE,"E38"),sQuery(id+"F12.wireOp",EDGE,"E39"),sQuery(id+"F12.wireOp",EDGE,"E41"),sQuery(id+"F12.wireOp",EDGE,"E42"),sQuery(id+"F12.wireOp",EDGE,"E43.MirrorCS"),sQuery(id+"F12.wireOp",EDGE,"E44.MirrorCS"),sQuery(id+"F12.wireOp",EDGE,"E45.MirrorCS"),sQuery(id+"F12.wireOp",EDGE,"E46.MirrorCS")])],"isStart":false})]});
            var Q5;
            Q5=makeQuery(id+"FJ3eJoukwGj3lDz_1.1.F13.boolean.opBoolean","COPY",EDGE,{"derivedFrom":makeQuery(id+"FJ3eJoukwGj3lDz_1.1.F13.opExtrude","SWEPT_EDGE",EDGE,{"disambiguationData":[OSD([sQuery(id+"F12.wireOp",EDGE,"E45.MirrorCS"),sQuery(id+"F12.wireOp",EDGE,"E46.MirrorCS")])]})});
            var Q6;
            Q6=makeQuery(id+"F13.boolean.opBoolean","COPY",EDGE,{"derivedFrom":makeQuery(id+"F13.opExtrude","SWEPT_EDGE",EDGE,{"disambiguationData":[OSD([sQuery(id+"F12.wireOp",EDGE,"E39"),sQuery(id+"F12.wireOp",EDGE,"E41")])]})});
            var Q7;
            Q7=makeQuery(id+"FJ3eJoukwGj3lDz_1.1.F13.boolean.opBoolean","COPY",EDGE,{"derivedFrom":makeQuery(id+"FJ3eJoukwGj3lDz_1.1.F13.opExtrude","SWEPT_EDGE",EDGE,{"disambiguationData":[OSD([sQuery(id+"F12.wireOp",EDGE,"E39"),sQuery(id+"F12.wireOp",EDGE,"E41")])]})});
            var Q8;
            Q8=makeQuery(id+"F13.boolean.opBoolean","COPY",EDGE,{"derivedFrom":makeQuery(id+"F13.opExtrude","SWEPT_EDGE",EDGE,{"disambiguationData":[OSD([sQuery(id+"F12.wireOp",EDGE,"E45.MirrorCS"),sQuery(id+"F12.wireOp",EDGE,"E46.MirrorCS")])]})});
            var Q9;
            Q9=makeQuery(id+"F13.boolean.opBoolean","INTERSECT",EDGE,{"derivedFrom":[makeQuery(id+"F3.boolean.opBoolean","COPY",FACE,{"derivedFrom":makeQuery(id+"F3.opExtrude","SWEPT_FACE",FACE,{"disambiguationData":[OSD([sQuery(id+"F0.wireOp",EDGE,"E0.left")])]})}),makeQuery(id+"F13.opExtrude","CAP_FACE",FACE,{"disambiguationData":[OSD([sQuery(id+"F12.wireOp",EDGE,"E38"),sQuery(id+"F12.wireOp",EDGE,"E39"),sQuery(id+"F12.wireOp",EDGE,"E41"),sQuery(id+"F12.wireOp",EDGE,"E42"),sQuery(id+"F12.wireOp",EDGE,"E43.MirrorCS"),sQuery(id+"F12.wireOp",EDGE,"E44.MirrorCS"),sQuery(id+"F12.wireOp",EDGE,"E45.MirrorCS"),sQuery(id+"F12.wireOp",EDGE,"E46.MirrorCS")])],"isStart":true})]});
            var Q10;
            Q10=makeQuery(id+"F13.boolean.opBoolean","INTERSECT",EDGE,{"derivedFrom":[makeQuery(id+"F3.boolean.opBoolean","COPY",FACE,{"derivedFrom":makeQuery(id+"F3.opExtrude","SWEPT_FACE",FACE,{"disambiguationData":[OSD([sQuery(id+"F0.wireOp",EDGE,"E0.left")])]})}),makeQuery(id+"F13.opExtrude","CAP_FACE",FACE,{"disambiguationData":[OSD([sQuery(id+"F12.wireOp",EDGE,"E38"),sQuery(id+"F12.wireOp",EDGE,"E39"),sQuery(id+"F12.wireOp",EDGE,"E41"),sQuery(id+"F12.wireOp",EDGE,"E42"),sQuery(id+"F12.wireOp",EDGE,"E43.MirrorCS"),sQuery(id+"F12.wireOp",EDGE,"E44.MirrorCS"),sQuery(id+"F12.wireOp",EDGE,"E45.MirrorCS"),sQuery(id+"F12.wireOp",EDGE,"E46.MirrorCS")])],"isStart":false})]});
            fillet(context, id + "F14", {"entities" : qUnion([Q0, Q1, Q2, Q3, Q4, Q5, Q6, Q7, Q8, Q9, Q10]), "radius" : 1 * mm, "tangentPropagation" : true, "allowEdgeOverflow" : false});
        }
        {
            var Q0;
            Q0=makeQuery(id+"F11.boolean.opBoolean","INTERSECT",EDGE,{"derivedFrom":[makeQuery(id+"F3.boolean.opBoolean","COPY",FACE,{"derivedFrom":makeQuery(id+"F3.opExtrude","SWEPT_FACE",FACE,{"disambiguationData":[OSD([sQuery(id+"F0.wireOp",EDGE,"E0.bottom")])]})}),makeQuery(id+"F11.opExtrude","CAP_FACE",FACE,{"disambiguationData":[OSD([sQuery(id+"F4.wireOp",EDGE,"E12.0"),sQuery(id+"F4.wireOp",EDGE,"E12.1"),sQuery(id+"F4.wireOp",EDGE,"E12.2"),sQuery(id+"F4.wireOp",EDGE,"E12.3"),sQuery(id+"F4.wireOp",EDGE,"E12.4"),sQuery(id+"F4.wireOp",EDGE,"E12.5"),sQuery(id+"F4.wireOp",EDGE,"E12.6"),sQuery(id+"F4.wireOp",EDGE,"E12.7"),sQuery(id+"F4.wireOp",EDGE,"E12.8"),sQuery(id+"F4.wireOp",EDGE,"E12.9"),sQuery(id+"F4.wireOp",EDGE,"E12.10"),sQuery(id+"F4.wireOp",EDGE,"E12.11"),sQuery(id+"F4.wireOp",EDGE,"E12.12"),sQuery(id+"F4.wireOp",EDGE,"E12.13"),sQuery(id+"F4.wireOp",EDGE,"E13.filletArc"),sQuery(id+"F4.wireOp",EDGE,"E14.filletArc"),sQuery(id+"F4.wireOp",EDGE,"E15.filletArc"),sQuery(id+"F4.wireOp",EDGE,"E16.filletArc"),sQuery(id+"F4.wireOp",EDGE,"E17.filletArc"),sQuery(id+"F4.wireOp",EDGE,"E18.filletArc"),sQuery(id+"F4.wireOp",EDGE,"E19.filletArc"),sQuery(id+"F4.wireOp",EDGE,"E20.filletArc"),sQuery(id+"F4.wireOp",EDGE,"E21.filletArc"),sQuery(id+"F4.wireOp",EDGE,"E22.filletArc"),sQuery(id+"F4.wireOp",EDGE,"E23.filletArc"),sQuery(id+"F4.wireOp",EDGE,"E24.filletArc"),sQuery(id+"F4.wireOp",EDGE,"E25.filletArc"),sQuery(id+"F4.wireOp",EDGE,"E26.filletArc")])],"isStart":false})]});
            var Q1;
            Q1=makeQuery(id+"F11.boolean.opBoolean","COPY",EDGE,{"derivedFrom":makeQuery(id+"F11.opExtrude","CAP_EDGE",EDGE,{"disambiguationData":[OSD([sQuery(id+"F4.wireOp",EDGE,"E12.10")])],"isStart":false})});
            fillet(context, id + "F15", {"entities" : qUnion([Q0, Q1]), "radius" : 2 * mm, "tangentPropagation" : true, "allowEdgeOverflow" : false});
        }
        {
            var Q0;
            Q0=makeQuery(id+"F3.boolean.opBoolean","COPY",EDGE,{"derivedFrom":makeQuery(id+"F3.opExtrude","CAP_EDGE",EDGE,{"disambiguationData":[OSD([sQuery(id+"F0.wireOp",EDGE,"E0.bottom")])],"isStart":true})});
            var Q1;
            Q1=makeQuery(id+"F11.boolean.opBoolean","COPY",EDGE,{"derivedFrom":makeQuery(id+"F11.opExtrude","CAP_EDGE",EDGE,{"disambiguationData":[OSD([sQuery(id+"F4.wireOp",EDGE,"E12.8")])],"isStart":true})});
            var Q2;
            Q2=makeQuery(id+"F7.opExtrude","CAP_EDGE",EDGE,{"disambiguationData":[OSD([sQuery(id+"F5.wireOp",EDGE,"E28.23")])],"isStart":true});
            chamfer(context, id + "F16", {"entities" : qUnion([Q0, Q1, Q2]), "width" : 0.6 * mm, "tangentPropagation" : true});
        }
        {
            var Q0;
            Q0=makeQuery(id+"F7.opExtrude","SWEPT_FACE",FACE,{"disambiguationData":[OSD([sQuery(id+"F5.wireOp",EDGE,"E28.18")])]});
            var sketch = newSketch(context, id + "F17", { "sketchPlane" : qUnion([Q0])});
            skCircle(sketch, "E48", {"center": v(0, 7) * mm, "radius": 3.5 * mm});
            skSolve(sketch);
        }
        {
            var Q0;
            Q0=makeQuery(id+"F17.imprint","IMPRINT",FACE,{"disambiguationData":[TD([[makeQuery(id+"F17.imprint","IMPRINT",EDGE,{"derivedFrom":sQuery(id+"F17.wireOp",EDGE,"E48")}),1.0]])]});
            extrude(context, id + "F18", {"entities" : qUnion([Q0]), "operationType" : NewBodyOperationType.REMOVE, "endBound" : BoundingType.THROUGH_ALL, "oppositeDirection" : true, "depth" : 25 * mm, "offsetDistance" : 25 * mm});
        }
    });
